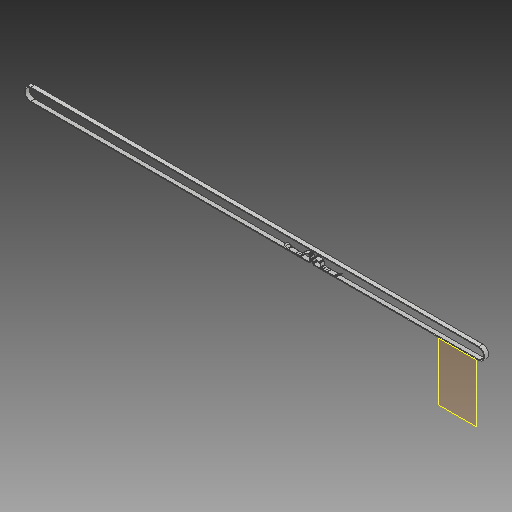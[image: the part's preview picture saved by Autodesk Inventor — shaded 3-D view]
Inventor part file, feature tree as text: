
AUTODESK INVENTOR PART (.ipt)
format: ipt  version: 2018 (Build 220112000, 112)  size: 210,432 bytes
history: native  units: mm
features: other x3, sketch x1, plane x1
ambient origin geometry x8: Origin, YZ Plane, XZ Plane, XY Plane, X Axis, Y Axis, Z Axis, Center Point
bodies: Solid1 (feature_tree)
feature tree (5):
  other  "XBELT.ipt"
  other  "Solid2::XBELT.ipt"
  other  "TaggingFeature1"
  sketch  "Sketch1"  dims[d0=10.0mm]
  plane  "Work Plane1"
